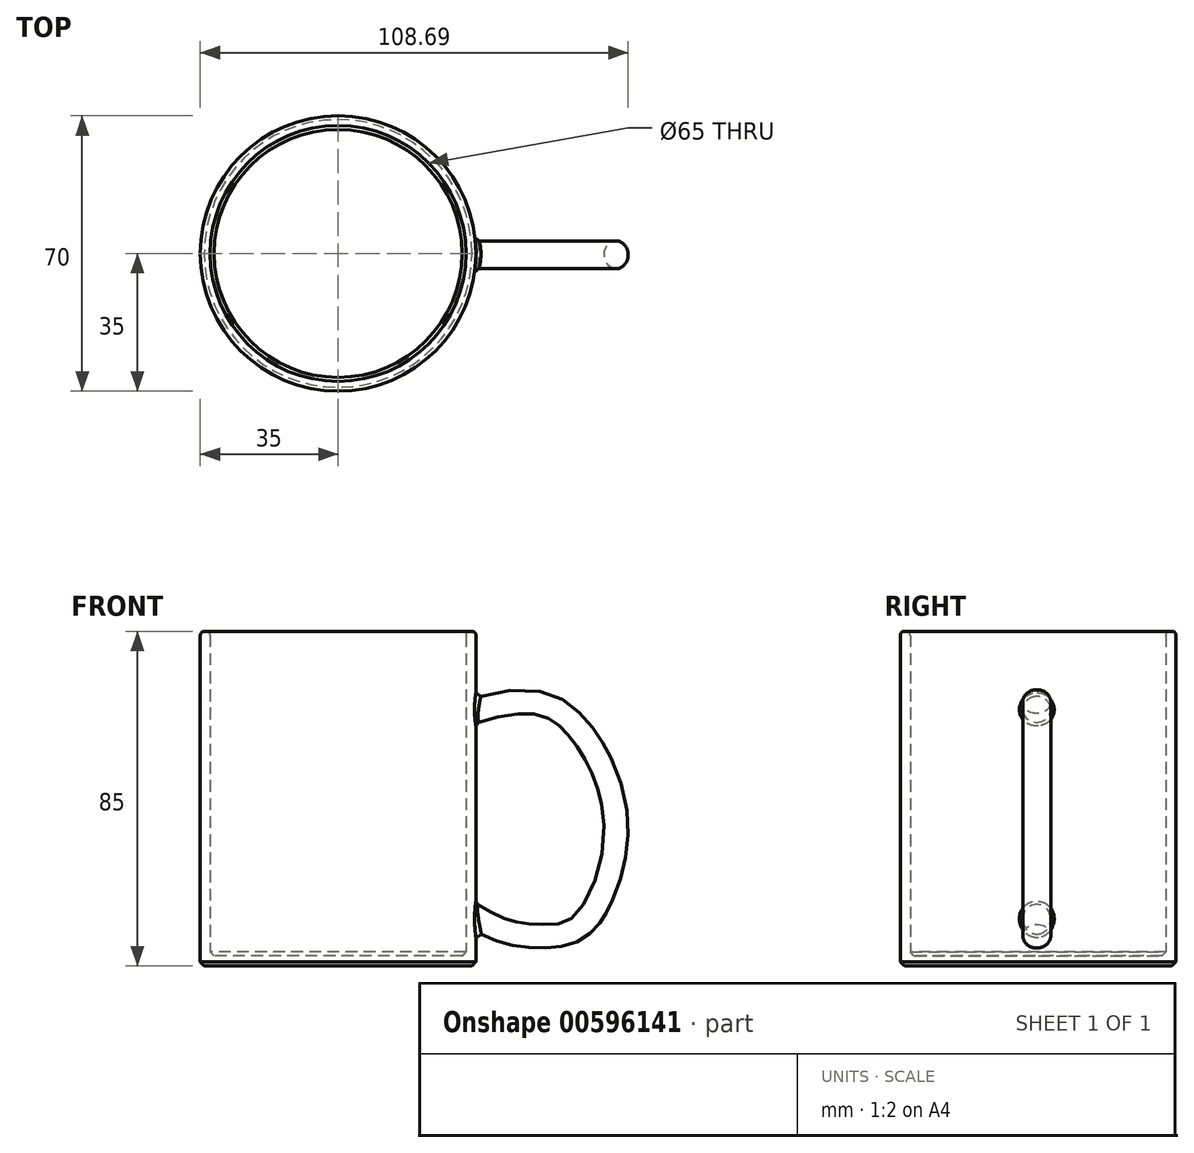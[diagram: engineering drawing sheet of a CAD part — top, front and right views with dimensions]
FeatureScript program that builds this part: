
annotation { "Feature Type Name" : "Feature", "Feature Type Description" : "" }
export const myFeature = defineFeature(function(context is Context, id is Id, definition is map)
    precondition{}
    {
        {
            var Q0;
            Q0=qCreatedBy(makeId("Top.planeOp"),FACE);
            var sketch = newSketch(context, id + "F0", { "sketchPlane" : qUnion([Q0])});
            skCircle(sketch, "E0", {"center": v(0, 0) * mm, "radius": 35 * mm});
            skSolve(sketch);
        }
        {
            var Q0;
            Q0 = qSketchRegion(id + "F0", true);
            var Q1;
            Q1=makeQuery(id+"F0.imprint","IMPRINT",FACE,{"disambiguationData":[TD([[makeQuery(id+"F0.imprint","IMPRINT",EDGE,{"derivedFrom":sQuery(id+"F0.wireOp",EDGE,"E0")}),1.0]])]});
            extrude(context, id + "F1", {"entities" : qUnion([Q0, Q1]), "depth" : 85 * mm, "offsetDistance" : 25 * mm});
        }
        {
            var Q0;
            Q0=qCreatedBy(makeId("Right.planeOp"),FACE);
            cPlane(context, id + "F2", {"entities" : qUnion([Q0]), "cplaneType" : CPlaneType.OFFSET, "offset" : 35 * mm, "width" : 150 * mm, "height" : 150 * mm});
        }
        {
            var Q0;
            Q0=qCreatedBy(makeId("Front.planeOp"),FACE);
            var sketch = newSketch(context, id + "F3", { "sketchPlane" : qUnion([Q0])});
            skFitSpline(sketch, "E1", {"points": [v(20.25, 59.51) * mm, v(48.92, 68.38) * mm, v(63.73, 58.95) * mm, v(71.96, 36.17) * mm, v(66.97, 14.9) * mm, v(59.3, 7.4) * mm, v(46.85, 6.5) * mm, v(32.35, 12.35) * mm], "startDerivative": vector(136.4, 84.31) * mm, "endDerivative": vector(-142.75, 90.05) * mm});
            skSolve(sketch);
        }
        {
            var Q0;
            Q0=qCreatedBy(id+"F2.planeOp",FACE);
            var sketch = newSketch(context, id + "F4", { "sketchPlane" : qUnion([Q0])});
            skCircle(sketch, "E2", {"center": v(-0.36, 12.35) * mm, "radius": 3.55 * mm});
            skPoint(sketch, "E2.first.point", {"position": v(-1.1, 15.82) * mm});
            skPoint(sketch, "E2.second.point", {"position": v(1.2, 9.16) * mm});
            skPoint(sketch, "E2.third.point", {"position": v(-2.02, 9.22) * mm});
            skSolve(sketch);
        }
        {
            var Q0;
            Q0=makeQuery(id+"F4.imprint","IMPRINT",FACE,{"disambiguationData":[TD([[makeQuery(id+"F4.imprint","IMPRINT",EDGE,{"derivedFrom":sQuery(id+"F4.wireOp",EDGE,"E2")}),1.0]])]});
            var Q1;
            Q1=sQuery(id+"F3.wireOp",EDGE,"E1");
            sweep(context, id + "F5", {"operationType" : NewBodyOperationType.ADD, "profiles" : qUnion([Q0]), "path" : qUnion([Q1])});
        }
        {
            var Q0;
            Q0=makeQuery(id+"F1.opExtrude","CAP_FACE",FACE,{"disambiguationData":[OSD([sQuery(id+"F0.wireOp",EDGE,"E0")])],"isStart":false});
            shell(context, id + "F6", {"entities" : qUnion([Q0]), "thickness" : 2.5 * mm});
        }
        {
            var Q0;
            {var subQ0=sQuery(id+"F0.wireOp",EDGE,"E0");Q0=makeQuery(id+"F6.opShell","OFFSET_EDGE",EDGE,{"disambiguationData":[OSD([subQ0]),TDD([makeQuery(id+"F1.opExtrude","CAP_EDGE",EDGE,{"disambiguationData":[OSD([subQ0])],"isStart":false})])]});}
            var Q1;
            Q1=makeQuery(id+"F1.opExtrude","CAP_EDGE",EDGE,{"disambiguationData":[OSD([sQuery(id+"F0.wireOp",EDGE,"E0")])],"isStart":false});
            fillet(context, id + "F7", {"entities" : qUnion([Q0, Q1]), "radius" : 1 * mm, "tangentPropagation" : true, "allowEdgeOverflow" : false});
        }
        {
            var Q0;
            Q0=makeQuery(id+"F5.opSweep","SWEPT_FACE",FACE,{"disambiguationData":[OSD([sQuery(id+"F3.wireOp",EDGE,"E1"),sQuery(id+"F4.wireOp",EDGE,"E2")])]});
            var Q1;
            Q1=makeQuery(id+"F1.opExtrude","CAP_EDGE",EDGE,{"disambiguationData":[OSD([sQuery(id+"F0.wireOp",EDGE,"E0")])],"isStart":true});
            var Q2;
            {var subQ0=sQuery(id+"F0.wireOp",EDGE,"E0");Q2=makeQuery(id+"F6.opShell","OFFSET_FACE",FACE,{"disambiguationData":[OSD([subQ0]),TDD([makeQuery(id+"F1.opExtrude","CAP_FACE",FACE,{"disambiguationData":[OSD([subQ0])],"isStart":true})])]});}
            chamfer(context, id + "F8", {"entities" : qUnion([Q0, Q1, Q2]), "width" : 1 * mm, "tangentPropagation" : true});
        }
    });
